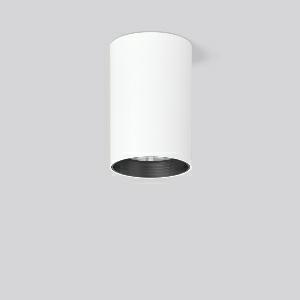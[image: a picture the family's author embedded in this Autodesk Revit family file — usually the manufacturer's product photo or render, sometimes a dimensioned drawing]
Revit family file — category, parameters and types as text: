
# Revit family: heledon_maxi_a_931220_002_1_4f1f
name_source: partatom
category: Lighting Fixtures
units: mm (PartAtom-declared; Revit-internal decimal feet)

## family parameters
Cut with Voids When Loaded = No
Host = Face
Light Source = No
Part Type = Normal
Room Calculation Point = No
Round Connector Dimension = Use Diameter
Shared = No

## types (1)
- HELEDON maxi A (1 x LED Modul 940, 3000 lm, 4000)
    Apparent Load = 25 VA
    Approval mark = CE
    CIE Flux Codes = 97 100 100 100 100
    Color Rendering = 92
    Color Temperature = 4000
    Default Elevation = 1800 mm
    Description = Series: HELEDON maxi
Cylindrical surface-mounted downlight. Housing: die-cast aluminium, powder-coated. Internal ceiling frame polycarbonate with bayonet mounting. Black plastic ring and recessed LED to prevent glare from the side. Optical assembly with lens made of plastic (polycarbonate) for the best homogeneous light distribution - can be changed without tools. Best colour rendering index Ra>90. Suitable for Ceiling mounting. Easy installation with a separate ceiling frame with bayonet mounting and plug connection. Driver integrated. Connected via plug-in connector. High quality converter without flickering and stroboscopic effect. The following accessories can be mounted without use of tools: interchangeable lenses, decorative glasses, honeycomb louvre, clear and frosted diffusers, white interchangeable plastic ring. 
Colour: traffic white, matt (RAL 9016)
Diameter: 123 mm
Height: 183 mm
Lamp: LED
Socket: without socket
Colour temperature: 4000K
Colour rendering index (CRI): 92
System power: 25 W
Rated luminous flux: 3000 lm
Luminous efficiency: 120 lm/W
Control gear: Regulated power supply
Protection class: I
Type of protection: IP 20
    Height = 183 mm
    Lamp = 1 x LED Modul 940
    Lamp Light Flux = 3000 lm
    Lamp count = 1
    Length = 123 mm
    Lifetime = 50000 h
    Luminous efficacy = 120 lm/W
    Manufacturer = RZB
    ModVariant = No
    Model = 931220.002.1
    Mounting Place = Ceiling
    Mounting Type = Surface mounted
    Number of Poles = 1
    OnlyDefault = Yes
    Power Factor = 1
    Product Name = HELEDON maxi A
    Product group = Surface mounted downlights
    ProductGroupID = 302
    Protection Class = Protection class I
    Protection Degree = IP 20
    RLX_Detail_Level = 1
    RLX_Emergency_Light_Flux = 0 lm
    RLX_Emergency_Type = 0
    RLX_Emergency_Type_DB = No
    RlxData = <blob elided: 97817 chars, md5=2762bb3c>
    Socket = socket
    Standby Power = 0 W
    System Light Flux = 3000 lm
    System Power = 25 W
    Type Comments = Product without accessories
    Type Image = 931193.002.jpg
    URL = http://relux.com
    VarID = ---
    Voltage = 230 V
    Voltage Range = 220-240 V
    Weight = 0.00 kg
    Width = 0 mm  [stored 0 ft]

note: [stored X ft] marks values corroborated as IEEE doubles in the binary element streams (Revit-internal decimal feet)

## geometry (parser evidence)
native form markers: Blend x4, Sweep x11
no freeform markers — native parametric forms only
